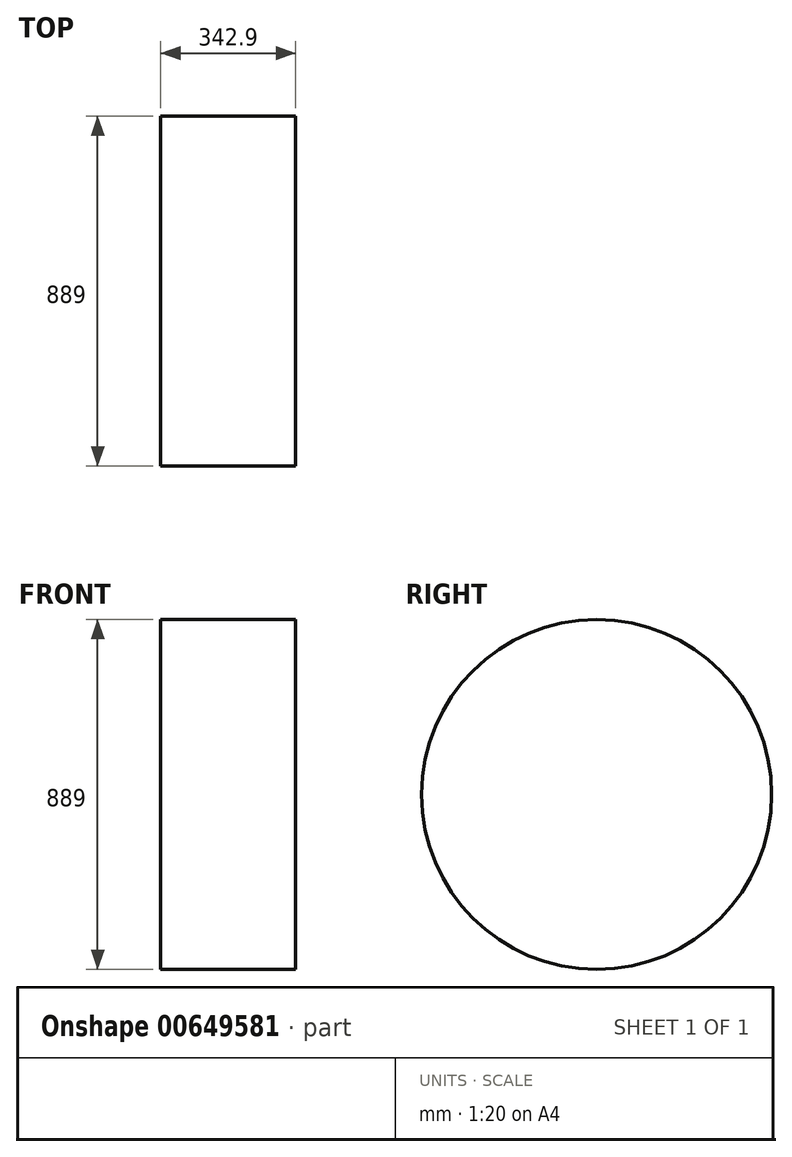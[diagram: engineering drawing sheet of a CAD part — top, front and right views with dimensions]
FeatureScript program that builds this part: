
annotation { "Feature Type Name" : "Feature", "Feature Type Description" : "" }
export const myFeature = defineFeature(function(context is Context, id is Id, definition is map)
    precondition{}
    {
        {
            var Q0;
            Q0=qCreatedBy(makeId("Right.planeOp"), FACE);
            var sketch = newSketch(context, id + "F0", { "sketchPlane" : qUnion([Q0])});
            skCircle(sketch, "E0", {"center": v(0, 0) * mm, "radius": 444.5 * mm});
            skSolve(sketch);
        }
        {
            var Q0;
            Q0 = qSketchRegion(id + "F0", true);
            extrude(context, id + "F1", {"entities" : qUnion([Q0]), "depth" : 342.9 * mm, "offsetDistance" : 25.4 * mm});
        }
    });
